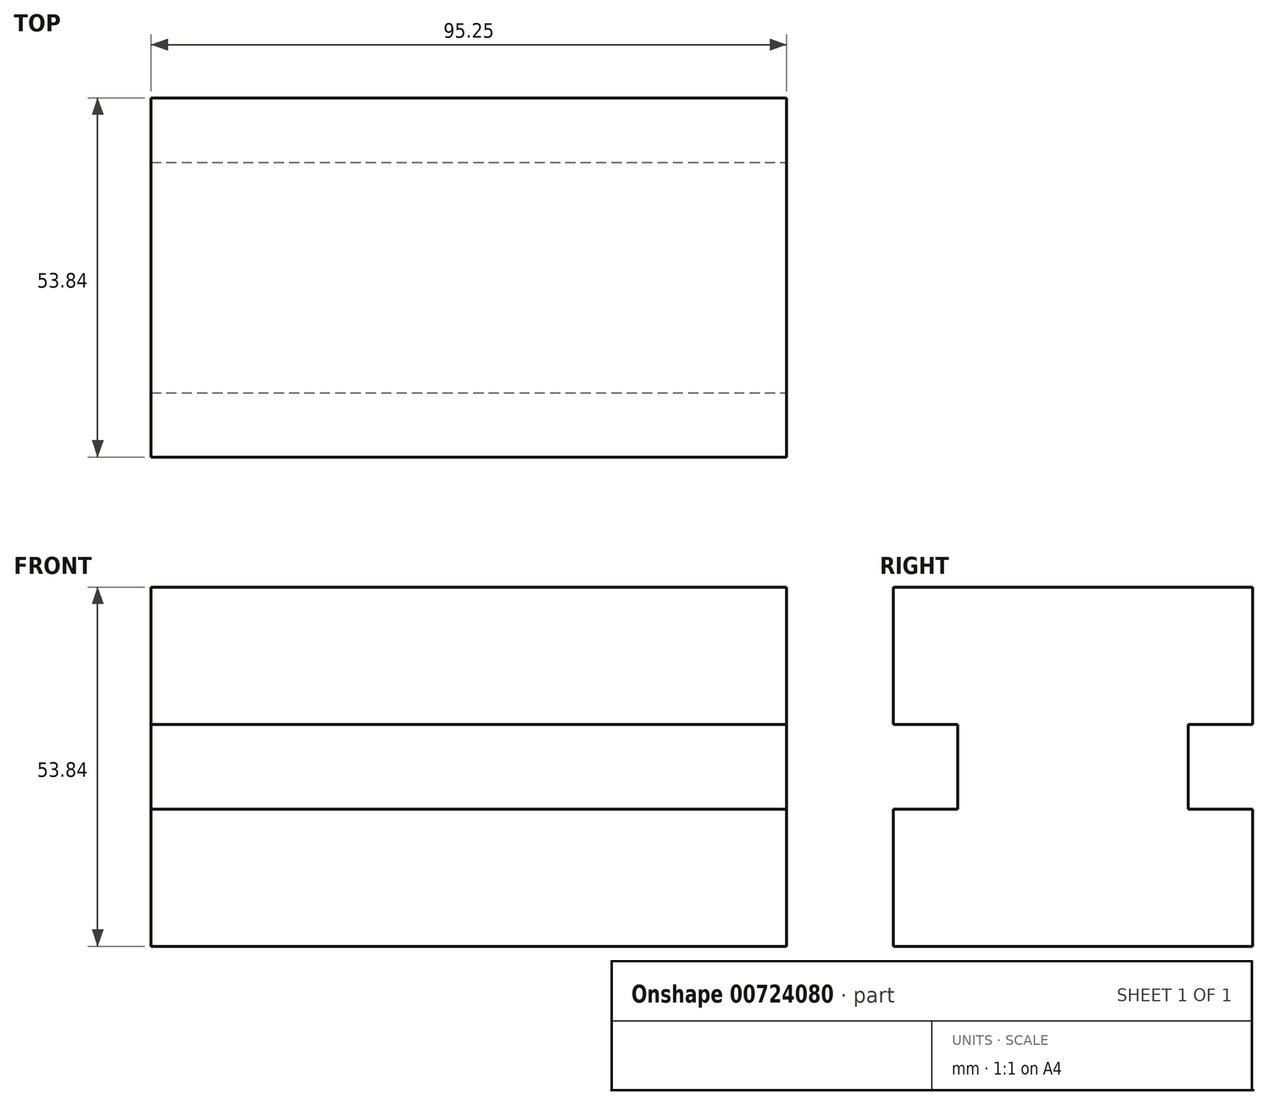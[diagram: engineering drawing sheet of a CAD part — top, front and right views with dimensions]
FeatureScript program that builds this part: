
annotation { "Feature Type Name" : "Feature", "Feature Type Description" : "" }
export const myFeature = defineFeature(function(context is Context, id is Id, definition is map)
    precondition{}
    {
        {
            var Q0;
            Q0=qCreatedBy(makeId("Right.planeOp"),FACE);
            var sketch = newSketch(context, id + "F0", { "sketchPlane" : qUnion([Q0])});
            skLineSegment(sketch, "E0.bottom", {"start": v(26.92, -26.92) * mm, "end": v(-26.92, -26.92) * mm});
            skLineSegment(sketch, "E0.top", {"start": v(26.92, 26.92) * mm, "end": v(-26.92, 26.92) * mm});
            skLineSegment(sketch, "E0.left", {"start": v(26.92, -26.92) * mm, "end": v(26.92, -6.35) * mm});
            skLineSegment(sketch, "E0.right", {"start": v(-26.92, -26.92) * mm, "end": v(-26.92, -6.35) * mm});
            skPoint(sketch, "E0.middle", {"position": v(0, 0) * mm});
            skLineSegment(sketch, "E1.bottom", {"start": v(-26.92, 6.35) * mm, "end": v(-17.27, 6.35) * mm});
            skLineSegment(sketch, "E1.top", {"start": v(-26.92, -6.35) * mm, "end": v(-17.27, -6.35) * mm});
            skLineSegment(sketch, "E1.right", {"start": v(-17.27, 6.35) * mm, "end": v(-17.27, -6.35) * mm});
            skLineSegment(sketch, "E2.trimOffspring", {"start": v(-26.92, 6.35) * mm, "end": v(-26.92, 26.92) * mm});
            skLineSegment(sketch, "E3", {"start": v(0, 43.38) * mm, "end": v(0, -50.12) * mm, "construction": true});
            skLineSegment(sketch, "E4.MirrorCS", {"start": v(26.92, 6.35) * mm, "end": v(17.27, 6.35) * mm});
            skLineSegment(sketch, "E5.MirrorCS", {"start": v(17.27, 6.35) * mm, "end": v(17.27, -6.35) * mm});
            skLineSegment(sketch, "E6.MirrorCS", {"start": v(26.92, -6.35) * mm, "end": v(17.27, -6.35) * mm});
            skLineSegment(sketch, "E7.trimOffspring", {"start": v(26.92, 6.35) * mm, "end": v(26.92, 26.92) * mm});
            skSolve(sketch);
        }
        {
            var Q0;
            Q0=makeQuery(id+"F0.imprint","IMPRINT",FACE,{"disambiguationData":[TD([[makeQuery(id+"F0.imprint","IMPRINT",EDGE,{"derivedFrom":sQuery(id+"F0.wireOp",EDGE,"E0.bottom")}),-1.0]])]});
            extrude(context, id + "F1", {"entities" : qUnion([Q0]), "oppositeDirection" : true, "depth" : 95.25 * mm, "offsetDistance" : 25.4 * mm});
        }
    });
